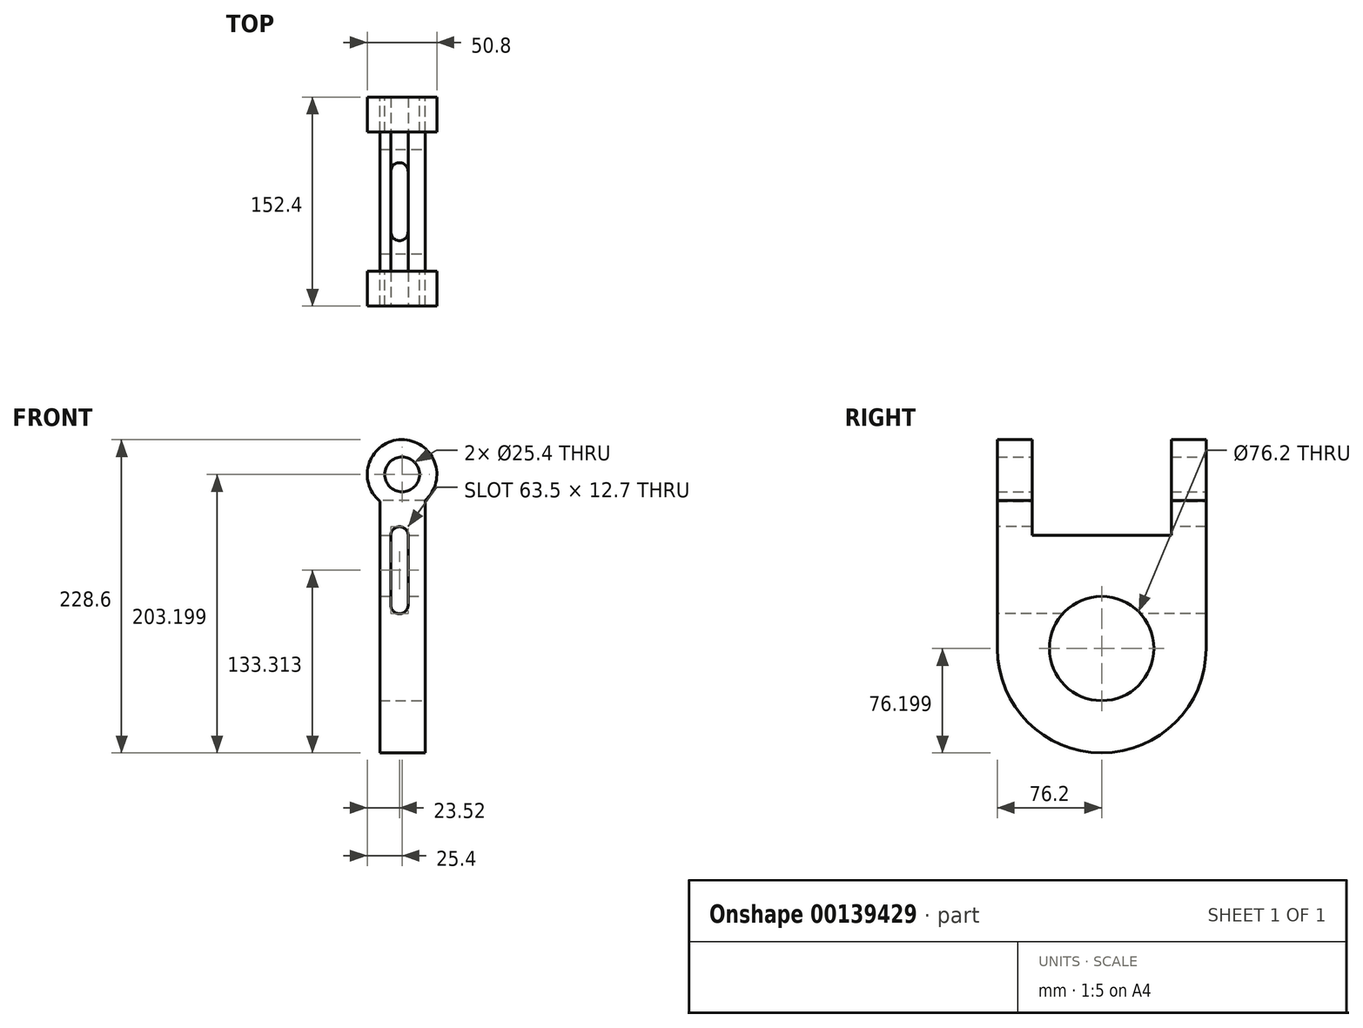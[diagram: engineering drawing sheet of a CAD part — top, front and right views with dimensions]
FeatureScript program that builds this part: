
annotation { "Feature Type Name" : "Feature", "Feature Type Description" : "" }
export const myFeature = defineFeature(function(context is Context, id is Id, definition is map)
    precondition{}
    {
        {
            var Q0;
            Q0=qCreatedBy(makeId("Front.planeOp"),FACE);
            var sketch = newSketch(context, id + "F0", { "sketchPlane" : qUnion([Q0])});
            skLineSegment(sketch, "E0", {"start": v(-20.73, 42.84) * mm, "end": v(-20.73, -140.85) * mm});
            skLineSegment(sketch, "E1", {"start": v(12.29, 43.26) * mm, "end": v(12.29, -140.85) * mm});
            skLineSegment(sketch, "E2", {"start": v(12.29, -140.85) * mm, "end": v(-20.73, -140.85) * mm});
            skCircle(sketch, "E3", {"center": v(-4.47, 62.35) * mm, "radius": 12.7 * mm});
            skArc(sketch, "E4", {"start": v(12.29, 43.26) * mm, "mid": v(-4.8, 87.75) * mm, "end": v(-20.73, 42.84) * mm});
            skSolve(sketch);
        }
        {
            var Q0;
            Q0 = qSketchRegion(id + "F0", true);
            extrude(context, id + "F1", {"entities" : qUnion([Q0]), "depth" : 152.4 * mm});
        }
        {
            var Q0;
            Q0=makeQuery(id+"F1.opExtrude","CAP_EDGE",EDGE,{"disambiguationData":[OSD([sQuery(id+"F0.wireOp",EDGE,"E2")])],"isStart":false});
            var Q1;
            Q1=makeQuery(id+"F1.opExtrude","CAP_EDGE",EDGE,{"disambiguationData":[OSD([sQuery(id+"F0.wireOp",EDGE,"E2")])],"isStart":true});
            fillet(context, id + "F2", {"entities" : qUnion([Q0, Q1]), "radius" : 76.2 * mm, "tangentPropagation" : true, "allowEdgeOverflow" : false});
        }
        {
            var Q0;
            Q0=makeQuery(id+"F1.opExtrude","SWEPT_FACE",FACE,{"disambiguationData":[OSD([sQuery(id+"F0.wireOp",EDGE,"E1")])]});
            var sketch = newSketch(context, id + "F3", { "sketchPlane" : qUnion([Q0])});
            skCircle(sketch, "E5", {"center": v(-76.2, -64.65) * mm, "radius": 38.1 * mm});
            skLineSegment(sketch, "E6", {"start": v(-127, 43.26) * mm, "end": v(-127, 17.86) * mm});
            skLineSegment(sketch, "E7", {"start": v(-127, 17.86) * mm, "end": v(-25.4, 17.86) * mm});
            skLineSegment(sketch, "E8", {"start": v(-25.4, 17.86) * mm, "end": v(-25.4, 43.26) * mm});
            skLineSegment(sketch, "E9", {"start": v(-25.4, 43.26) * mm, "end": v(0, 43.26) * mm});
            skLineSegment(sketch, "E10", {"start": v(0, 43.26) * mm, "end": v(0, 17.86) * mm});
            skLineSegment(sketch, "E11", {"start": v(-127, 43.26) * mm, "end": v(-152.4, 43.26) * mm});
            skSolve(sketch);
        }
        {
            var Q0;
            Q0 = qSketchRegion(id + "F3", true);
            extrude(context, id + "F4", {"entities" : qUnion([Q0]), "operationType" : NewBodyOperationType.REMOVE, "endBound" : BoundingType.THROUGH_ALL, "oppositeDirection" : true, "depth" : 25.4 * mm});
        }
        {
            var Q0;
            {var subQ0=sQuery(id+"F3.wireOp",EDGE,"E6");Q0=makeQuery(id+"F3.imprint","IMPRINT",FACE,{"disambiguationData":[TD([[makeQuery(id+"F3.imprint","IMPRINT",EDGE,{"derivedFrom":subQ0}),1.0]])]});}
            extrude(context, id + "F5", {"entities" : qUnion([Q0]), "operationType" : NewBodyOperationType.REMOVE, "endBound" : BoundingType.THROUGH_ALL, "oppositeDirection" : true, "depth" : 25.4 * mm});
        }
        {
            var Q0;
            Q0=makeQuery(id+"F1.opExtrude","SWEPT_FACE",FACE,{"disambiguationData":[OSD([sQuery(id+"F0.wireOp",EDGE,"E0")])]});
            var sketch = newSketch(context, id + "F6", { "sketchPlane" : qUnion([Q0])});
            skLineSegment(sketch, "E12.bottom", {"start": v(127, 17.86) * mm, "end": v(25.43, 17.86) * mm});
            skLineSegment(sketch, "E12.top", {"start": v(127, 109.78) * mm, "end": v(25.43, 109.78) * mm});
            skLineSegment(sketch, "E12.left", {"start": v(127, 17.86) * mm, "end": v(127, 109.78) * mm});
            skLineSegment(sketch, "E12.right", {"start": v(25.43, 17.86) * mm, "end": v(25.43, 109.78) * mm});
            skSolve(sketch);
        }
        {
            var Q0;
            {var subQ5=sQuery(id+"F6.wireOp",EDGE,"E12.bottom");Q0=makeQuery(id+"F6.imprint","IMPRINT",FACE,{"disambiguationData":[TD([[makeQuery(id+"F6.imprint","IMPRINT",EDGE,{"derivedFrom":subQ5}),-1.0]])]});}
            extrude(context, id + "F7", {"entities" : qUnion([Q0]), "operationType" : NewBodyOperationType.REMOVE, "endBound" : BoundingType.SYMMETRIC, "oppositeDirection" : true, "depth" : 90.58 * mm});
        }
        {
            var Q0;
            Q0=makeQuery(id+"F1.opExtrude","CAP_FACE",FACE,{"disambiguationData":[OSD([sQuery(id+"F0.wireOp",EDGE,"E0"),sQuery(id+"F0.wireOp",EDGE,"E1"),sQuery(id+"F0.wireOp",EDGE,"E2"),sQuery(id+"F0.wireOp",EDGE,"E3"),sQuery(id+"F0.wireOp",EDGE,"E4")])],"isStart":false});
            var sketch = newSketch(context, id + "F8", { "sketchPlane" : qUnion([Q0])});
            skArc(sketch, "E13", {"start": v(0, 17.86) * mm, "mid": v(-6.35, 24.21) * mm, "end": v(-12.7, 17.86) * mm});
            skLineSegment(sketch, "E14", {"start": v(0, 17.86) * mm, "end": v(0, -32.94) * mm});
            skLineSegment(sketch, "E15", {"start": v(-12.7, 17.86) * mm, "end": v(-12.7, -32.94) * mm});
            skArc(sketch, "E16", {"start": v(-12.7, -32.94) * mm, "mid": v(-6.35, -39.29) * mm, "end": v(0, -32.94) * mm});
            skSolve(sketch);
        }
        {
            var Q0;
            Q0 = qSketchRegion(id + "F8", true);
            extrude(context, id + "F9", {"entities" : qUnion([Q0]), "operationType" : NewBodyOperationType.REMOVE, "endBound" : BoundingType.THROUGH_ALL, "oppositeDirection" : true, "depth" : 25.4 * mm});
        }
    });
